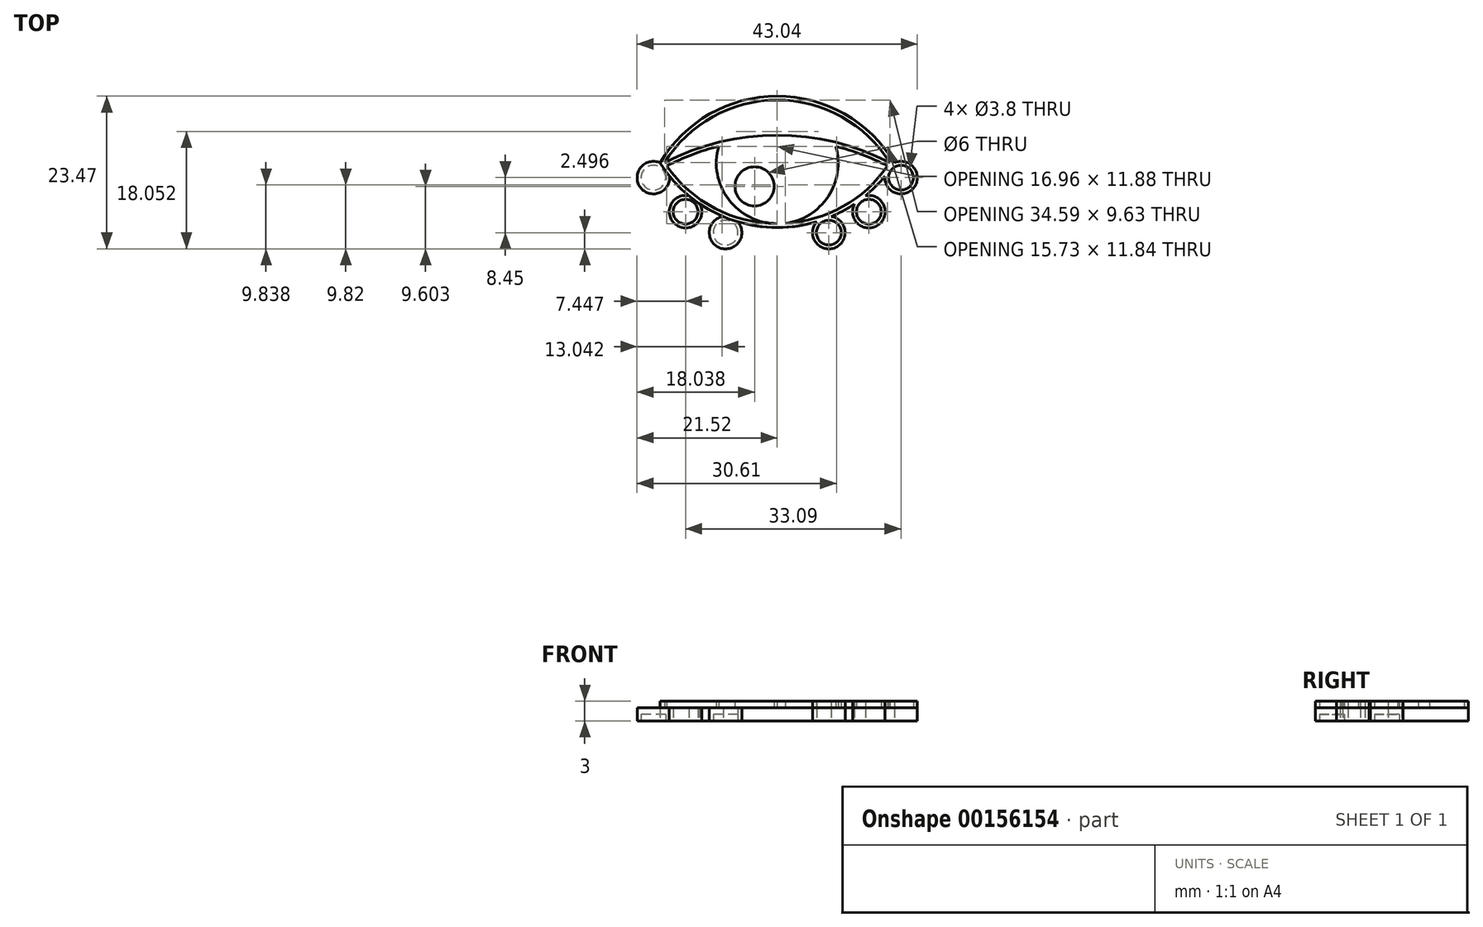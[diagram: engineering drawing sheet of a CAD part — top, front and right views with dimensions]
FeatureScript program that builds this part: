
annotation { "Feature Type Name" : "Feature", "Feature Type Description" : "" }
export const myFeature = defineFeature(function(context is Context, id is Id, definition is map)
    precondition{}
    {
        {
            var Q0;
            Q0=qCreatedBy(makeId("Top.planeOp"),FACE);
            var sketch = newSketch(context, id + "F0", { "sketchPlane" : qUnion([Q0])});
            skLineSegment(sketch, "E0", {"start": v(-18, 5.83) * mm, "end": v(-18, -9) * mm, "construction": true});
            skLineSegment(sketch, "E1", {"start": v(18, 6.72) * mm, "end": v(18, -10.09) * mm, "construction": true});
            skLineSegment(sketch, "E2", {"start": v(-16.76, 10) * mm, "end": v(10.92, 10) * mm, "construction": true});
            skLineSegment(sketch, "E3", {"start": v(-13.9, -10) * mm, "end": v(10.53, -10) * mm, "construction": true});
            skArc(sketch, "E4", {"start": v(18, 0) * mm, "mid": v(0, 10.24) * mm, "end": v(-18, 0) * mm});
            skArc(sketch, "E5", {"start": v(-18, 0) * mm, "mid": v(-4.4, -9.49) * mm, "end": v(11.88, -6.32) * mm});
            skLineSegment(sketch, "E6", {"start": v(-17.68, 5) * mm, "end": v(30.6, 5) * mm, "construction": true});
            skCircle(sketch, "E7", {"center": v(-3.48, -3.63) * mm, "radius": 3 * mm});
            skArc(sketch, "E8", {"start": v(-1.11, -9.92) * mm, "mid": v(0.04, -14.66) * mm, "end": v(1.04, -9.89) * mm});
            skArc(sketch, "E9", {"start": v(6.07, -9.07) * mm, "mid": v(8.8, -13.08) * mm, "end": v(8.24, -8.25) * mm});
            skArc(sketch, "E10", {"start": v(11.88, -6.32) * mm, "mid": v(15.57, -9.52) * mm, "end": v(13.55, -5.07) * mm});
            skArc(sketch, "E11", {"start": v(16.53, -2.06) * mm, "mid": v(21.05, -3.74) * mm, "end": v(18, 0) * mm});
            skArc(sketch, "E12.0", {"start": v(17.3, 0) * mm, "mid": v(0, 9.64) * mm, "end": v(-17.3, 0) * mm});
            skArc(sketch, "E12.1", {"start": v(-17.3, 0) * mm, "mid": v(-17.13, -0.24) * mm, "end": v(-16.95, -0.5) * mm});
            skArc(sketch, "E13", {"start": v(17.3, 0) * mm, "mid": v(0, 4.25) * mm, "end": v(-17.3, 0) * mm});
            skArc(sketch, "E14.0", {"start": v(16.96, -0.5) * mm, "mid": v(13.07, 1.25) * mm, "end": v(9, 2.53) * mm});
            skArc(sketch, "E15", {"start": v(-9, 2.53) * mm, "mid": v(-7.45, -5.65) * mm, "end": v(0, -9.35) * mm});
            skArc(sketch, "E16", {"start": v(16.53, -2.06) * mm, "mid": v(17.3, -1.05) * mm, "end": v(18, 0) * mm});
            skCircle(sketch, "E17", {"center": v(19.02, -2.28) * mm, "radius": 1.9 * mm});
            skCircle(sketch, "E18", {"center": v(14.07, -7.52) * mm, "radius": 1.9 * mm});
            skCircle(sketch, "E19", {"center": v(7.93, -10.73) * mm, "radius": 1.9 * mm});
            skCircle(sketch, "E20", {"center": v(0, -12.16) * mm, "radius": 1.9 * mm});
            skArc(sketch, "E21.MirrorCS", {"start": v(-16.53, -2.06) * mm, "mid": v(-21.05, -3.74) * mm, "end": v(-18, 0) * mm});
            skCircle(sketch, "E22.MirrorC", {"center": v(-19.02, -2.28) * mm, "radius": 1.9 * mm});
            skArc(sketch, "E23.MirrorCS", {"start": v(-11.88, -6.32) * mm, "mid": v(-15.57, -9.52) * mm, "end": v(-13.55, -5.07) * mm});
            skCircle(sketch, "E24.MirrorC", {"center": v(-14.07, -7.52) * mm, "radius": 1.9 * mm});
            skArc(sketch, "E25.MirrorCS", {"start": v(-6.07, -9.07) * mm, "mid": v(-8.8, -13.08) * mm, "end": v(-8.24, -8.25) * mm});
            skCircle(sketch, "E26.MirrorC", {"center": v(-7.93, -10.73) * mm, "radius": 1.9 * mm});
            skArc(sketch, "E27.MirrorCS", {"start": v(1.11, -9.92) * mm, "mid": v(-0.04, -14.66) * mm, "end": v(-1.04, -9.89) * mm});
            skArc(sketch, "E28", {"start": v(-9, 2.53) * mm, "mid": v(-13.07, 1.25) * mm, "end": v(-16.96, -0.5) * mm});
            skArc(sketch, "E29", {"start": v(9, 2.53) * mm, "mid": v(0, 3.65) * mm, "end": v(-9, 2.53) * mm});
            skLineSegment(sketch, "E30", {"start": v(0, -9.35) * mm, "end": v(0, -9.35) * mm});
            skArc(sketch, "E31", {"start": v(0, -9.35) * mm, "mid": v(0.61, -9.34) * mm, "end": v(1.22, -9.31) * mm});
            skArc(sketch, "E32.0", {"start": v(17.74, -0.15) * mm, "mid": v(0, 9.94) * mm, "end": v(-17.74, -0.15) * mm, "construction": true});
            skArc(sketch, "E33.0", {"start": v(17.13, -0.25) * mm, "mid": v(0, 3.95) * mm, "end": v(-17.13, -0.25) * mm, "construction": true});
            skArc(sketch, "E34", {"start": v(11.88, -6.32) * mm, "mid": v(12.73, -5.72) * mm, "end": v(13.55, -5.07) * mm});
            skArc(sketch, "E35", {"start": v(13.55, -5.07) * mm, "mid": v(15.11, -3.64) * mm, "end": v(16.53, -2.06) * mm});
            skArc(sketch, "E36", {"start": v(1.22, -9.31) * mm, "mid": v(7.83, -5.17) * mm, "end": v(9, 2.53) * mm});
            skArc(sketch, "E37", {"start": v(1.22, -9.31) * mm, "mid": v(10.1, -6.71) * mm, "end": v(16.96, -0.5) * mm});
            skArc(sketch, "E38", {"start": v(-16.95, -0.5) * mm, "mid": v(-9.56, -7) * mm, "end": v(0, -9.35) * mm});
            skArc(sketch, "E39", {"start": v(16.96, -0.5) * mm, "mid": v(17.13, -0.24) * mm, "end": v(17.3, 0) * mm});
            skSolve(sketch);
        }
        {
            var Q0;
            Q0=makeQuery(id+"F0.imprint","IMPRINT",FACE,{"disambiguationData":[TD([[makeQuery(id+"F0.imprint","IMPRINT",EDGE,{"derivedFrom":sQuery(id+"F0.wireOp",EDGE,"E19")}),-1.0]])]});
            var Q1;
            Q1=makeQuery(id+"F0.imprint","IMPRINT",FACE,{"disambiguationData":[TD([[makeQuery(id+"F0.imprint","IMPRINT",EDGE,{"derivedFrom":sQuery(id+"F0.wireOp",EDGE,"E19")}),1.0]])]});
            var Q2;
            {var subQ0=sQuery(id+"F0.wireOp",EDGE,"E23.MirrorCS");Q2=makeQuery(id+"F0.imprint","IMPRINT",FACE,{"disambiguationData":[TD([[makeQuery(id+"F0.imprint","IMPRINT",EDGE,{"derivedFrom":subQ0}),-1.0]])]});}
            var Q3;
            Q3=makeQuery(id+"F0.imprint","IMPRINT",FACE,{"disambiguationData":[TD([[makeQuery(id+"F0.imprint","IMPRINT",EDGE,{"derivedFrom":sQuery(id+"F0.wireOp",EDGE,"E24.MirrorC")}),-1.0]])]});
            var Q4;
            Q4=makeQuery(id+"F0.imprint","IMPRINT",FACE,{"disambiguationData":[TD([[makeQuery(id+"F0.imprint","IMPRINT",EDGE,{"derivedFrom":sQuery(id+"F0.wireOp",EDGE,"E7")}),-1.0]])]});
            var Q5;
            Q5=makeQuery(id+"F0.imprint","IMPRINT",FACE,{"disambiguationData":[TD([[makeQuery(id+"F0.imprint","IMPRINT",EDGE,{"derivedFrom":sQuery(id+"F0.wireOp",EDGE,"E22.MirrorC")}),-1.0]])]});
            var Q6;
            Q6=makeQuery(id+"F0.imprint","IMPRINT",FACE,{"disambiguationData":[TD([[makeQuery(id+"F0.imprint","IMPRINT",EDGE,{"derivedFrom":sQuery(id+"F0.wireOp",EDGE,"E12.0")}),1.0]])]});
            var Q7;
            {var subQ0=sQuery(id+"F0.wireOp",EDGE,"532d2993-fab8-4ee6-9c43-ea5b56531bbd");Q7=makeQuery(id+"F0.imprint","IMPRINT",FACE,{"disambiguationData":[TD([[makeQuery(id+"F0.imprint","IMPRINT",EDGE,{"derivedFrom":subQ0}),-1.0]])]});}
            var Q8;
            Q8=makeQuery(id+"F0.imprint","IMPRINT",FACE,{"disambiguationData":[TD([[makeQuery(id+"F0.imprint","IMPRINT",EDGE,{"derivedFrom":sQuery(id+"F0.wireOp",EDGE,"E26.MirrorC")}),1.0]])]});
            var Q9;
            Q9=makeQuery(id+"F0.imprint","IMPRINT",FACE,{"disambiguationData":[TD([[makeQuery(id+"F0.imprint","IMPRINT",EDGE,{"derivedFrom":sQuery(id+"F0.wireOp",EDGE,"E7")}),1.0]])]});
            var Q10;
            {var subQ0=sQuery(id+"F0.wireOp",EDGE,"E15");Q10=makeQuery(id+"F0.imprint","IMPRINT",FACE,{"disambiguationData":[TD([[makeQuery(id+"F0.imprint","IMPRINT",EDGE,{"derivedFrom":subQ0}),-1.0]])]});}
            var Q11;
            Q11=makeQuery(id+"F0.imprint","IMPRINT",FACE,{"disambiguationData":[TD([[makeQuery(id+"F0.imprint","IMPRINT",EDGE,{"derivedFrom":sQuery(id+"F0.wireOp",EDGE,"E20")}),1.0]])]});
            var Q12;
            Q12=makeQuery(id+"F0.imprint","IMPRINT",FACE,{"disambiguationData":[TD([[makeQuery(id+"F0.imprint","IMPRINT",EDGE,{"derivedFrom":sQuery(id+"F0.wireOp",EDGE,"E17")}),1.0]])]});
            var Q13;
            {var subQ4=sQuery(id+"F0.wireOp",EDGE,"E4");Q13=makeQuery(id+"F0.imprint","IMPRINT",FACE,{"disambiguationData":[TD([[makeQuery(id+"F0.imprint","IMPRINT",EDGE,{"derivedFrom":subQ4}),1.0]])]});}
            var Q14;
            {var subQ7=sQuery(id+"F0.wireOp",EDGE,"E13");Q14=makeQuery(id+"F0.imprint","IMPRINT",FACE,{"disambiguationData":[TD([[makeQuery(id+"F0.imprint","IMPRINT",EDGE,{"derivedFrom":subQ7}),1.0]])]});}
            var Q15;
            {var subQ0=sQuery(id+"F0.wireOp",EDGE,"E16");Q15=makeQuery(id+"F0.imprint","IMPRINT",FACE,{"disambiguationData":[TD([[makeQuery(id+"F0.imprint","IMPRINT",EDGE,{"derivedFrom":subQ0}),-1.0]])]});}
            var Q16;
            Q16=makeQuery(id+"F0.imprint","IMPRINT",FACE,{"disambiguationData":[TD([[makeQuery(id+"F0.imprint","IMPRINT",EDGE,{"derivedFrom":sQuery(id+"F0.wireOp",EDGE,"E10")}),1.0]])]});
            var Q17;
            Q17=makeQuery(id+"F0.imprint","IMPRINT",FACE,{"disambiguationData":[TD([[makeQuery(id+"F0.imprint","IMPRINT",EDGE,{"derivedFrom":sQuery(id+"F0.wireOp",EDGE,"E22.MirrorC")}),1.0]])]});
            var Q18;
            Q18=makeQuery(id+"F0.imprint","IMPRINT",FACE,{"disambiguationData":[TD([[makeQuery(id+"F0.imprint","IMPRINT",EDGE,{"derivedFrom":sQuery(id+"F0.wireOp",EDGE,"E26.MirrorC")}),-1.0]])]});
            var Q19;
            Q19=makeQuery(id+"F0.imprint","IMPRINT",FACE,{"disambiguationData":[TD([[makeQuery(id+"F0.imprint","IMPRINT",EDGE,{"derivedFrom":sQuery(id+"F0.wireOp",EDGE,"E18")}),1.0]])]});
            var Q20;
            Q20=makeQuery(id+"F0.imprint","IMPRINT",FACE,{"disambiguationData":[TD([[makeQuery(id+"F0.imprint","IMPRINT",EDGE,{"derivedFrom":sQuery(id+"F0.wireOp",EDGE,"E20")}),-1.0]])]});
            var Q21;
            Q21=makeQuery(id+"F0.imprint","IMPRINT",FACE,{"disambiguationData":[TD([[makeQuery(id+"F0.imprint","IMPRINT",EDGE,{"derivedFrom":sQuery(id+"F0.wireOp",EDGE,"E14.0")}),1.0]])]});
            extrude(context, id + "F1", {"entities" : qUnion([Q0, Q1, Q2, Q3, Q4, Q5, Q6, Q7, Q8, Q9, Q10, Q11, Q12, Q13, Q14, Q15, Q16, Q17, Q18, Q19, Q20, Q21]), "depth" : 2 * mm});
        }
        {
            var Q0;
            {var subQ4=sQuery(id+"F0.wireOp",EDGE,"E4");Q0=makeQuery(id+"F0.imprint","IMPRINT",FACE,{"disambiguationData":[TD([[makeQuery(id+"F0.imprint","IMPRINT",EDGE,{"derivedFrom":subQ4}),1.0]])]});}
            var Q1;
            Q1=makeQuery(id+"F0.imprint","IMPRINT",FACE,{"disambiguationData":[TD([[makeQuery(id+"F0.imprint","IMPRINT",EDGE,{"derivedFrom":sQuery(id+"F0.wireOp",EDGE,"E22.MirrorC")}),1.0]])]});
            var Q2;
            {var subQ0=sQuery(id+"F0.wireOp",EDGE,"E23.MirrorCS");Q2=makeQuery(id+"F0.imprint","IMPRINT",FACE,{"disambiguationData":[TD([[makeQuery(id+"F0.imprint","IMPRINT",EDGE,{"derivedFrom":subQ0}),-1.0]])]});}
            var Q3;
            Q3=makeQuery(id+"F0.imprint","IMPRINT",FACE,{"disambiguationData":[TD([[makeQuery(id+"F0.imprint","IMPRINT",EDGE,{"derivedFrom":sQuery(id+"F0.wireOp",EDGE,"E26.MirrorC")}),1.0]])]});
            var Q4;
            Q4=makeQuery(id+"F0.imprint","IMPRINT",FACE,{"disambiguationData":[TD([[makeQuery(id+"F0.imprint","IMPRINT",EDGE,{"derivedFrom":sQuery(id+"F0.wireOp",EDGE,"E20")}),1.0]])]});
            var Q5;
            Q5=makeQuery(id+"F0.imprint","IMPRINT",FACE,{"disambiguationData":[TD([[makeQuery(id+"F0.imprint","IMPRINT",EDGE,{"derivedFrom":sQuery(id+"F0.wireOp",EDGE,"E19")}),-1.0]])]});
            var Q6;
            Q6=makeQuery(id+"F0.imprint","IMPRINT",FACE,{"disambiguationData":[TD([[makeQuery(id+"F0.imprint","IMPRINT",EDGE,{"derivedFrom":sQuery(id+"F0.wireOp",EDGE,"E10")}),1.0]])]});
            var Q7;
            {var subQ0=sQuery(id+"F0.wireOp",EDGE,"E16");Q7=makeQuery(id+"F0.imprint","IMPRINT",FACE,{"disambiguationData":[TD([[makeQuery(id+"F0.imprint","IMPRINT",EDGE,{"derivedFrom":subQ0}),-1.0]])]});}
            var Q8;
            {var subQ1=sQuery(id+"F0.wireOp",EDGE,"E13");Q8=makeQuery(id+"F0.imprint","IMPRINT",FACE,{"disambiguationData":[TD([[makeQuery(id+"F0.imprint","IMPRINT",EDGE,{"derivedFrom":subQ1}),1.0]])]});}
            var Q9;
            Q9=makeQuery(id+"F0.imprint","IMPRINT",FACE,{"disambiguationData":[TD([[makeQuery(id+"F0.imprint","IMPRINT",EDGE,{"derivedFrom":sQuery(id+"F0.wireOp",EDGE,"E7")}),-1.0]])]});
            extrude(context, id + "F2", {"entities" : qUnion([Q0, Q1, Q2, Q3, Q4, Q5, Q6, Q7, Q8, Q9]), "depth" : 1 * mm});
        }
        {
            var Q0;
            Q0=makeQuery(id+"F2.opExtrude","SWEPT_BODY",BODY,{"disambiguationData":[OSD([sQuery(id+"F0.wireOp",EDGE,"E4"),sQuery(id+"F0.wireOp",EDGE,"E5"),sQuery(id+"F0.wireOp",EDGE,"E7"),sQuery(id+"F0.wireOp",EDGE,"E9"),sQuery(id+"F0.wireOp",EDGE,"E10"),sQuery(id+"F0.wireOp",EDGE,"E11"),sQuery(id+"F0.wireOp",EDGE,"E12.0"),sQuery(id+"F0.wireOp",EDGE,"E12.1"),sQuery(id+"F0.wireOp",EDGE,"E13"),sQuery(id+"F0.wireOp",EDGE,"E14.0"),sQuery(id+"F0.wireOp",EDGE,"E15"),sQuery(id+"F0.wireOp",EDGE,"E17"),sQuery(id+"F0.wireOp",EDGE,"E18"),sQuery(id+"F0.wireOp",EDGE,"E19"),sQuery(id+"F0.wireOp",EDGE,"E21.MirrorCS"),sQuery(id+"F0.wireOp",EDGE,"E22.MirrorC"),sQuery(id+"F0.wireOp",EDGE,"E23.MirrorCS"),sQuery(id+"F0.wireOp",EDGE,"E24.MirrorC"),sQuery(id+"F0.wireOp",EDGE,"E25.MirrorCS"),sQuery(id+"F0.wireOp",EDGE,"E26.MirrorC"),sQuery(id+"F0.wireOp",EDGE,"E27.MirrorCS"),sQuery(id+"F0.wireOp",EDGE,"E20"),sQuery(id+"F0.wireOp",EDGE,"E28"),sQuery(id+"F0.wireOp",EDGE,"E35"),sQuery(id+"F0.wireOp",EDGE,"E36"),sQuery(id+"F0.wireOp",EDGE,"E37"),sQuery(id+"F0.wireOp",EDGE,"E38")])]});
            transform(context, id + "F3", {"entities" : qUnion([Q0]), "transformType" : TransformType.TRANSLATION_3D, "dx" : 0 * mm, "dy" : 0 * mm, "dz" : 2 * mm, "makeCopy" : false});
        }
    });
